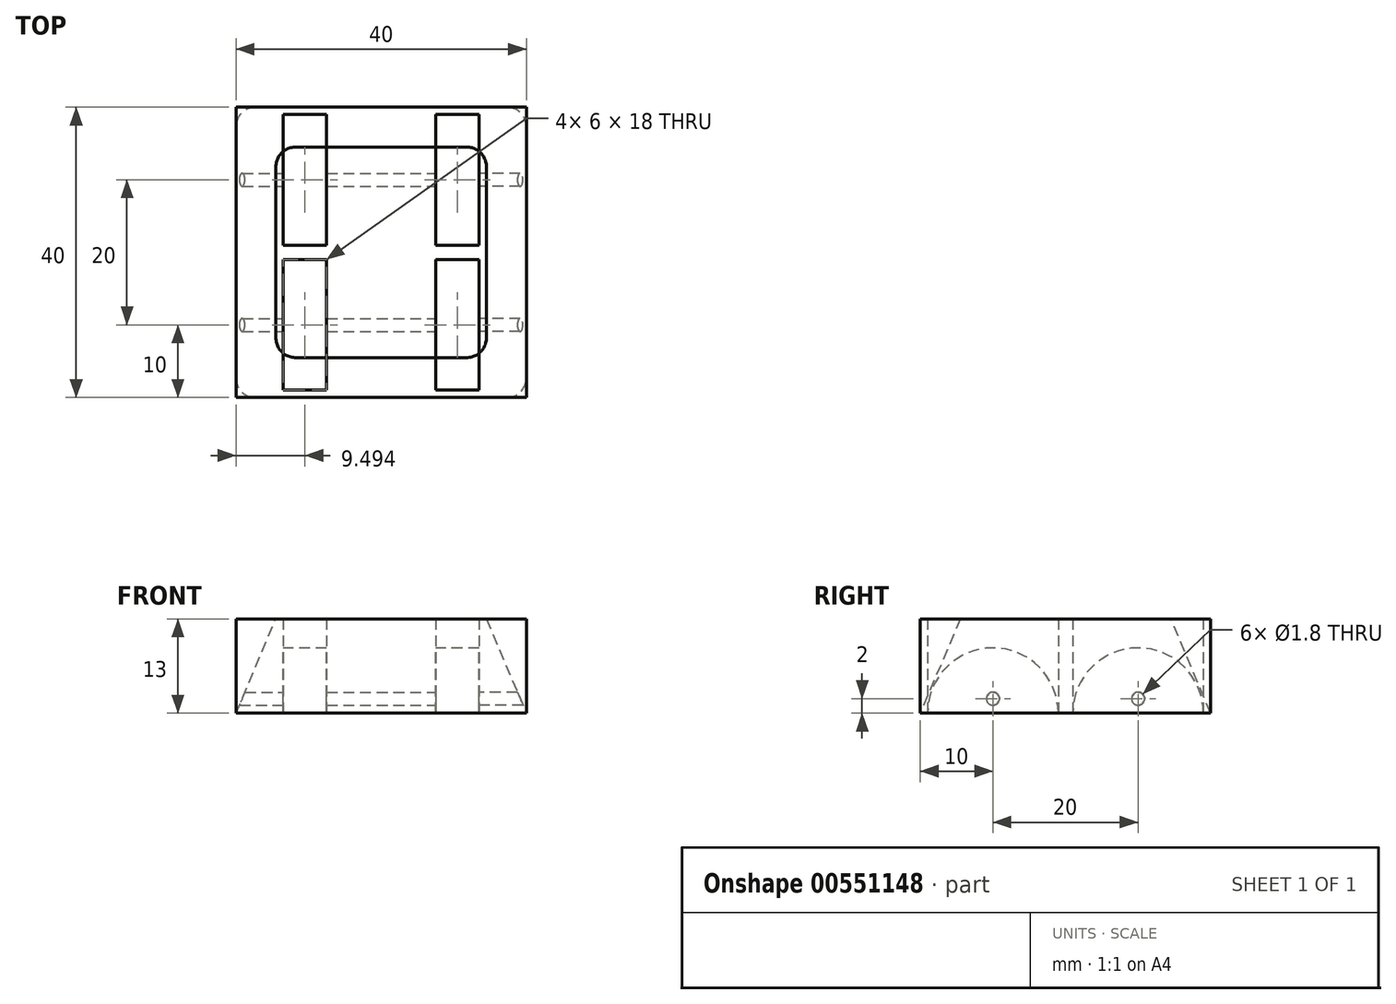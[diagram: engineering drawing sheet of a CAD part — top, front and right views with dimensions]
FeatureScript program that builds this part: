
annotation { "Feature Type Name" : "Feature", "Feature Type Description" : "" }
export const myFeature = defineFeature(function(context is Context, id is Id, definition is map)
    precondition{}
    {
        {
            var Q0;
            Q0=qCreatedBy(makeId("Top.planeOp"),FACE);
            var sketch = newSketch(context, id + "F0", { "sketchPlane" : qUnion([Q0])});
            skLineSegment(sketch, "E0.bottom", {"start": v(20, -20) * mm, "end": v(-20, -20) * mm});
            skLineSegment(sketch, "E0.top", {"start": v(20, 20) * mm, "end": v(-20, 20) * mm});
            skLineSegment(sketch, "E0.left", {"start": v(20, -20) * mm, "end": v(20, 20) * mm});
            skLineSegment(sketch, "E0.right", {"start": v(-20, -20) * mm, "end": v(-20, 20) * mm});
            skPoint(sketch, "E0.middle", {"position": v(0, 0) * mm});
            skLineSegment(sketch, "E1", {"start": v(-7.5, 19) * mm, "end": v(-7.5, 1) * mm});
            skLineSegment(sketch, "E2", {"start": v(-7.5, -19) * mm, "end": v(-7.5, -1) * mm});
            skLineSegment(sketch, "E3", {"start": v(7.5, -19) * mm, "end": v(7.5, -1) * mm});
            skLineSegment(sketch, "E4.bottom", {"start": v(13.5, -1) * mm, "end": v(7.5, -1) * mm});
            skLineSegment(sketch, "E4.top", {"start": v(13.5, -19) * mm, "end": v(7.5, -19) * mm});
            skLineSegment(sketch, "E4.right", {"start": v(7.5, -1) * mm, "end": v(7.5, -19) * mm});
            skLineSegment(sketch, "E5.bottom", {"start": v(13.5, 1) * mm, "end": v(7.5, 1) * mm});
            skLineSegment(sketch, "E5.top", {"start": v(13.5, 19) * mm, "end": v(7.5, 19) * mm});
            skLineSegment(sketch, "E6.bottom", {"start": v(-7.5, 1) * mm, "end": v(-13.5, 1) * mm});
            skLineSegment(sketch, "E6.left", {"start": v(-7.5, 1) * mm, "end": v(-7.5, 19) * mm});
            skLineSegment(sketch, "E7.bottom", {"start": v(-13.5, -1) * mm, "end": v(-7.5, -1) * mm});
            skLineSegment(sketch, "E7.top", {"start": v(-13.5, -19) * mm, "end": v(-7.5, -19) * mm});
            skLineSegment(sketch, "E7.right", {"start": v(-7.5, -1) * mm, "end": v(-7.5, -19) * mm});
            skPoint(sketch, "E8", {"position": v(-13.5, -10) * mm});
            skPoint(sketch, "E9", {"position": v(-7.5, -10) * mm});
            skPoint(sketch, "E10", {"position": v(7.5, -10) * mm});
            skPoint(sketch, "E11", {"position": v(13.5, -10) * mm});
            skPoint(sketch, "E12", {"position": v(13.5, 10) * mm});
            skPoint(sketch, "E13", {"position": v(7.5, 10) * mm});
            skPoint(sketch, "E14", {"position": v(-7.5, 10) * mm});
            skPoint(sketch, "E15", {"position": v(-13.5, 10) * mm});
            skLineSegment(sketch, "E16", {"start": v(-13.5, 10) * mm, "end": v(-7.5, 10) * mm, "construction": true});
            skLineSegment(sketch, "E17", {"start": v(7.5, 10) * mm, "end": v(13.5, 10) * mm, "construction": true});
            skLineSegment(sketch, "E18", {"start": v(7.5, -10) * mm, "end": v(13.5, -10) * mm, "construction": true});
            skLineSegment(sketch, "E19", {"start": v(-13.5, -10) * mm, "end": v(-7.5, -10) * mm, "construction": true});
            skLineSegment(sketch, "E20", {"start": v(-13.5, 19) * mm, "end": v(-7.5, 19) * mm});
            skLineSegment(sketch, "E21", {"start": v(13.5, -10) * mm, "end": v(7.5, -10) * mm});
            skLineSegment(sketch, "E22", {"start": v(-7.5, -10) * mm, "end": v(-13.5, -10) * mm});
            skLineSegment(sketch, "E23", {"start": v(-7.5, 10) * mm, "end": v(-13.5, 10) * mm});
            skLineSegment(sketch, "E24", {"start": v(7.5, 10) * mm, "end": v(13.5, 10) * mm});
            skPoint(sketch, "E25", {"position": v(-20, -10) * mm});
            skPoint(sketch, "E26", {"position": v(20, -10) * mm});
            skPoint(sketch, "E27", {"position": v(-20, 10) * mm});
            skPoint(sketch, "E28", {"position": v(20, 10) * mm});
            skLineSegment(sketch, "E29", {"start": v(13.5, -1) * mm, "end": v(13.5, -19) * mm, "construction": true});
            skLineSegment(sketch, "E30", {"start": v(13.5, 19) * mm, "end": v(13.5, 1) * mm, "construction": true});
            skLineSegment(sketch, "E31", {"start": v(-13.5, 19) * mm, "end": v(-13.5, 1) * mm, "construction": true});
            skLineSegment(sketch, "E32", {"start": v(-13.5, -1) * mm, "end": v(-13.5, -19) * mm, "construction": true});
            skLineSegment(sketch, "E33", {"start": v(7.5, 19) * mm, "end": v(7.5, 1) * mm, "construction": true});
            skLineSegment(sketch, "E34", {"start": v(13.5, -1) * mm, "end": v(13.5, -19) * mm});
            skLineSegment(sketch, "E35", {"start": v(13.5, 19) * mm, "end": v(13.5, 1) * mm});
            skLineSegment(sketch, "E36", {"start": v(-13.5, 19) * mm, "end": v(-13.5, 1) * mm});
            skLineSegment(sketch, "E37", {"start": v(-13.5, -1) * mm, "end": v(-13.5, -19) * mm});
            skLineSegment(sketch, "E38", {"start": v(7.5, 19) * mm, "end": v(7.5, 1) * mm});
            skSolve(sketch);
        }
        {
            var Q0;
            Q0=qCreatedBy(makeId("Right.planeOp"),FACE);
            var sketch = newSketch(context, id + "F1", { "sketchPlane" : qUnion([Q0])});
            skLineSegment(sketch, "E39", {"start": v(0, 0) * mm, "end": v(0, 13) * mm});
            skLineSegment(sketch, "E40", {"start": v(0, 0) * mm, "end": v(20, 0) * mm});
            skLineSegment(sketch, "E41", {"start": v(0, 0) * mm, "end": v(-20, 0) * mm});
            skLineSegment(sketch, "E42", {"start": v(0, 13) * mm, "end": v(-14.5, 13) * mm});
            skLineSegment(sketch, "E43", {"start": v(0, 13) * mm, "end": v(14.5, 13) * mm});
            skLineSegment(sketch, "E44", {"start": v(-14.5, 13) * mm, "end": v(-20, 0) * mm});
            skLineSegment(sketch, "E45", {"start": v(14.5, 13) * mm, "end": v(20, 0) * mm});
            skLineSegment(sketch, "E46", {"start": v(-14.5, 13) * mm, "end": v(-20, 0) * mm, "construction": true});
            skLineSegment(sketch, "E47", {"start": v(-20, 0) * mm, "end": v(20, 0) * mm, "construction": true});
            skLineSegment(sketch, "E48", {"start": v(20, 0) * mm, "end": v(14.5, 13) * mm, "construction": true});
            skLineSegment(sketch, "E49", {"start": v(10, 0) * mm, "end": v(10, 2) * mm});
            skLineSegment(sketch, "E50", {"start": v(-10, 0) * mm, "end": v(-10, 2) * mm});
            skCircle(sketch, "E51", {"center": v(-10, 2) * mm, "radius": 0.9 * mm});
            skLineSegment(sketch, "E52", {"start": v(10, 0) * mm, "end": v(10, 0.2) * mm});
            skLineSegment(sketch, "E53", {"start": v(10, 2) * mm, "end": v(10, 1) * mm});
            skCircle(sketch, "E54", {"center": v(10, 2) * mm, "radius": 0.9 * mm});
            skSolve(sketch);
        }
        {
            var Q0;
            Q0=qCreatedBy(makeId("Top.planeOp"),FACE);
            var sketch = newSketch(context, id + "F2", { "sketchPlane" : qUnion([Q0])});
            skLineSegment(sketch, "E55", {"start": v(20, -20) * mm, "end": v(20, 20) * mm});
            skLineSegment(sketch, "E56", {"start": v(20, 20) * mm, "end": v(-20, 20) * mm});
            skLineSegment(sketch, "E57", {"start": v(-20, 20) * mm, "end": v(-20, -20) * mm});
            skLineSegment(sketch, "E58", {"start": v(-20, -20) * mm, "end": v(20, -20) * mm});
            skLineSegment(sketch, "E59", {"start": v(0, 0) * mm, "end": v(0, -20) * mm});
            skLineSegment(sketch, "E60", {"start": v(0, 0) * mm, "end": v(-20, 0) * mm});
            skSolve(sketch);
        }
        {
            var Q0;
            Q0 = qSketchRegion(id + "F2", true);
            extrude(context, id + "F3", {"entities" : qUnion([Q0]), "depth" : 13 * mm, "offsetDistance" : 25.4 * mm});
        }
        {
            var Q0;
            {var subQ0=sQuery(id+"F0.wireOp",EDGE,"E20");Q0=makeQuery(id+"F0.imprint","IMPRINT",FACE,{"disambiguationData":[TD([[makeQuery(id+"F0.imprint","IMPRINT",EDGE,{"derivedFrom":subQ0}),-1.0]])]});}
            var Q1;
            Q1=sQuery(id+"F0.wireOp",EDGE,"E23");
            revolve(context, id + "F4", {"operationType" : NewBodyOperationType.REMOVE, "entities" : qUnion([Q0]), "axis" : qUnion([Q1]), "revolveType" : RevolveType.FULL, "oppositeDirection" : true});
        }
        {
            var Q0;
            {var subQ0=sQuery(id+"F0.wireOp",EDGE,"E4.bottom");Q0=makeQuery(id+"F0.imprint","IMPRINT",FACE,{"disambiguationData":[TD([[makeQuery(id+"F0.imprint","IMPRINT",EDGE,{"derivedFrom":subQ0}),1.0]])]});}
            var Q1;
            Q1=sQuery(id+"F0.wireOp",EDGE,"E21");
            revolve(context, id + "F5", {"operationType" : NewBodyOperationType.REMOVE, "entities" : qUnion([Q0]), "axis" : qUnion([Q1]), "revolveType" : RevolveType.FULL, "oppositeDirection" : true});
        }
        {
            var Q0;
            {var subQ0=sQuery(id+"F0.wireOp",EDGE,"E7.bottom");Q0=makeQuery(id+"F0.imprint","IMPRINT",FACE,{"disambiguationData":[TD([[makeQuery(id+"F0.imprint","IMPRINT",EDGE,{"derivedFrom":subQ0}),-1.0]])]});}
            var Q1;
            Q1=sQuery(id+"F0.wireOp",EDGE,"E22");
            revolve(context, id + "F6", {"operationType" : NewBodyOperationType.REMOVE, "entities" : qUnion([Q0]), "axis" : qUnion([Q1]), "revolveType" : RevolveType.FULL, "oppositeDirection" : true});
        }
        {
            var Q0;
            {var subQ0=sQuery(id+"F0.wireOp",EDGE,"E5.top");Q0=makeQuery(id+"F0.imprint","IMPRINT",FACE,{"disambiguationData":[TD([[makeQuery(id+"F0.imprint","IMPRINT",EDGE,{"derivedFrom":subQ0}),1.0]])]});}
            var Q1;
            Q1=sQuery(id+"F0.wireOp",EDGE,"E24");
            revolve(context, id + "F7", {"operationType" : NewBodyOperationType.REMOVE, "entities" : qUnion([Q0]), "axis" : qUnion([Q1]), "revolveType" : RevolveType.FULL, "oppositeDirection" : true});
        }
        {
            var Q0;
            Q0=makeQuery(id+"F3.opExtrude","CAP_EDGE",EDGE,{"disambiguationData":[OSD([sQuery(id+"F2.wireOp",EDGE,"E55")])],"isStart":false});
            chamfer(context, id + "F8", {"entities" : qUnion([Q0]), "chamferType" : ChamferType.TWO_OFFSETS, "width1" : 13 * mm, "oppositeDirection" : true, "width2" : 5.5 * mm, "tangentPropagation" : true});
        }
        {
            var Q0;
            Q0=makeQuery(id+"F3.opExtrude","CAP_EDGE",EDGE,{"disambiguationData":[OSD([sQuery(id+"F2.wireOp",EDGE,"E56")])],"isStart":false});
            chamfer(context, id + "F9", {"entities" : qUnion([Q0]), "chamferType" : ChamferType.TWO_OFFSETS, "width1" : 5.5 * mm, "oppositeDirection" : false, "width2" : 13 * mm, "tangentPropagation" : true});
        }
        {
            var Q0;
            Q0=makeQuery(id+"F3.opExtrude","CAP_EDGE",EDGE,{"disambiguationData":[OSD([sQuery(id+"F2.wireOp",EDGE,"E57")])],"isStart":false});
            chamfer(context, id + "F10", {"entities" : qUnion([Q0]), "chamferType" : ChamferType.TWO_OFFSETS, "width1" : 5.5 * mm, "oppositeDirection" : false, "width2" : 13 * mm, "tangentPropagation" : true});
        }
        {
            var Q0;
            Q0=makeQuery(id+"F3.opExtrude","CAP_EDGE",EDGE,{"disambiguationData":[OSD([sQuery(id+"F2.wireOp",EDGE,"E58")])],"isStart":false});
            chamfer(context, id + "F11", {"entities" : qUnion([Q0]), "chamferType" : ChamferType.TWO_OFFSETS, "width1" : 5.5 * mm, "oppositeDirection" : false, "width2" : 13 * mm, "tangentPropagation" : true});
        }
        {
            var Q0;
            Q0=sQuery(id+"F1.wireOp",VERTEX,"E54.center");
            var Q1;
            Q1=makeQuery(id+"F3.opExtrude","SWEPT_BODY",BODY,{"disambiguationData":[OSD([sQuery(id+"F2.wireOp",EDGE,"E55"),sQuery(id+"F2.wireOp",EDGE,"E56"),sQuery(id+"F2.wireOp",EDGE,"E57"),sQuery(id+"F2.wireOp",EDGE,"E58")])]});
            hole(context, id + "F12", {"style" : HoleStyle.SIMPLE, "endStyle" : HoleEndStyle.THROUGH, "holeDiameter" : 1.8 * mm, "isTappedThrough" : true, "tappedDepth" : 12.7 * mm, "tapClearance" : 3, "locations" : qUnion([Q0]), "scope" : qUnion([Q1])});
        }
        {
            var Q0;
            Q0=sQuery(id+"F1.wireOp",VERTEX,"E54.center");
            var Q1;
            Q1=makeQuery(id+"F3.opExtrude","SWEPT_BODY",BODY,{"disambiguationData":[OSD([sQuery(id+"F2.wireOp",EDGE,"E55"),sQuery(id+"F2.wireOp",EDGE,"E56"),sQuery(id+"F2.wireOp",EDGE,"E57"),sQuery(id+"F2.wireOp",EDGE,"E58")])]});
            hole(context, id + "F13", {"style" : HoleStyle.SIMPLE, "endStyle" : HoleEndStyle.THROUGH, "oppositeDirection" : true, "holeDiameter" : 1.8 * mm, "isTappedThrough" : true, "tappedDepth" : 12.7 * mm, "tapClearance" : 3, "locations" : qUnion([Q0]), "scope" : qUnion([Q1])});
        }
        {
            var Q0;
            Q0=sQuery(id+"F1.wireOp",VERTEX,"E50.end");
            var Q1;
            Q1=makeQuery(id+"F3.opExtrude","SWEPT_BODY",BODY,{"disambiguationData":[OSD([sQuery(id+"F2.wireOp",EDGE,"E55"),sQuery(id+"F2.wireOp",EDGE,"E56"),sQuery(id+"F2.wireOp",EDGE,"E57"),sQuery(id+"F2.wireOp",EDGE,"E58")])]});
            hole(context, id + "F14", {"style" : HoleStyle.SIMPLE, "endStyle" : HoleEndStyle.THROUGH, "holeDiameter" : 1.8 * mm, "isTappedThrough" : true, "tappedDepth" : 12.7 * mm, "tapClearance" : 3, "locations" : qUnion([Q0]), "scope" : qUnion([Q1])});
        }
        {
            var Q0;
            Q0=sQuery(id+"F1.wireOp",VERTEX,"E50.end");
            var Q1;
            Q1=makeQuery(id+"F3.opExtrude","SWEPT_BODY",BODY,{"disambiguationData":[OSD([sQuery(id+"F2.wireOp",EDGE,"E55"),sQuery(id+"F2.wireOp",EDGE,"E56"),sQuery(id+"F2.wireOp",EDGE,"E57"),sQuery(id+"F2.wireOp",EDGE,"E58")])]});
            hole(context, id + "F15", {"style" : HoleStyle.SIMPLE, "endStyle" : HoleEndStyle.THROUGH, "oppositeDirection" : true, "holeDiameter" : 1.8 * mm, "isTappedThrough" : true, "tappedDepth" : 12.7 * mm, "tapClearance" : 3, "locations" : qUnion([Q0]), "scope" : qUnion([Q1])});
        }
        {
            var Q0;
            Q0=makeQuery(id+"F11.opChamfer","BLEND_EDGE",EDGE,{"blendedFrom":[makeQuery(id+"F3.opExtrude","CAP_EDGE",EDGE,{"disambiguationData":[OSD([sQuery(id+"F2.wireOp",EDGE,"E58")])],"isStart":false}),makeQuery(id+"F10.opChamfer","BLEND_FACE",FACE,{"disambiguationData":[OSD([sQuery(id+"F2.wireOp",EDGE,"E57")])]})],"blendedInto":[makeQuery(id+"F10.opChamfer","BLEND_FACE",FACE,{"disambiguationData":[OSD([sQuery(id+"F2.wireOp",EDGE,"E57")])]})]});
            var Q1;
            Q1=makeQuery(id+"F10.opChamfer","BLEND_EDGE",EDGE,{"blendedFrom":[makeQuery(id+"F3.opExtrude","CAP_EDGE",EDGE,{"disambiguationData":[OSD([sQuery(id+"F2.wireOp",EDGE,"E57")])],"isStart":false}),makeQuery(id+"F9.opChamfer","BLEND_FACE",FACE,{"disambiguationData":[OSD([sQuery(id+"F2.wireOp",EDGE,"E56")])]})],"blendedInto":[makeQuery(id+"F9.opChamfer","BLEND_FACE",FACE,{"disambiguationData":[OSD([sQuery(id+"F2.wireOp",EDGE,"E56")])]})]});
            var Q2;
            Q2=makeQuery(id+"F9.opChamfer","BLEND_EDGE",EDGE,{"blendedFrom":[makeQuery(id+"F3.opExtrude","CAP_EDGE",EDGE,{"disambiguationData":[OSD([sQuery(id+"F2.wireOp",EDGE,"E56")])],"isStart":false}),makeQuery(id+"F8.opChamfer","BLEND_FACE",FACE,{"disambiguationData":[OSD([sQuery(id+"F2.wireOp",EDGE,"E55")])]})],"blendedInto":[makeQuery(id+"F8.opChamfer","BLEND_FACE",FACE,{"disambiguationData":[OSD([sQuery(id+"F2.wireOp",EDGE,"E55")])]})]});
            var Q3;
            Q3=makeQuery(id+"F11.opChamfer","BLEND_EDGE",EDGE,{"blendedFrom":[makeQuery(id+"F3.opExtrude","CAP_EDGE",EDGE,{"disambiguationData":[OSD([sQuery(id+"F2.wireOp",EDGE,"E58")])],"isStart":false}),makeQuery(id+"F8.opChamfer","BLEND_FACE",FACE,{"disambiguationData":[OSD([sQuery(id+"F2.wireOp",EDGE,"E55")])]})],"blendedInto":[makeQuery(id+"F8.opChamfer","BLEND_FACE",FACE,{"disambiguationData":[OSD([sQuery(id+"F2.wireOp",EDGE,"E55")])]})]});
            fillet(context, id + "F16", {"entities" : qUnion([Q0, Q1, Q2, Q3]), "radius" : 3 * mm, "tangentPropagation" : true, "allowEdgeOverflow" : false});
        }
        {
            var Q0;
            Q0=makeQuery(id+"F0.imprint","IMPRINT",FACE,{"disambiguationData":[TD([[makeQuery(id+"F0.imprint","IMPRINT",EDGE,{"derivedFrom":sQuery(id+"F0.wireOp",EDGE,"E0.bottom")}),-1.0]])]});
            extrude(context, id + "F17", {"entities" : qUnion([Q0]), "depth" : 13 * mm, "offsetDistance" : 25.4 * mm});
        }
    });
